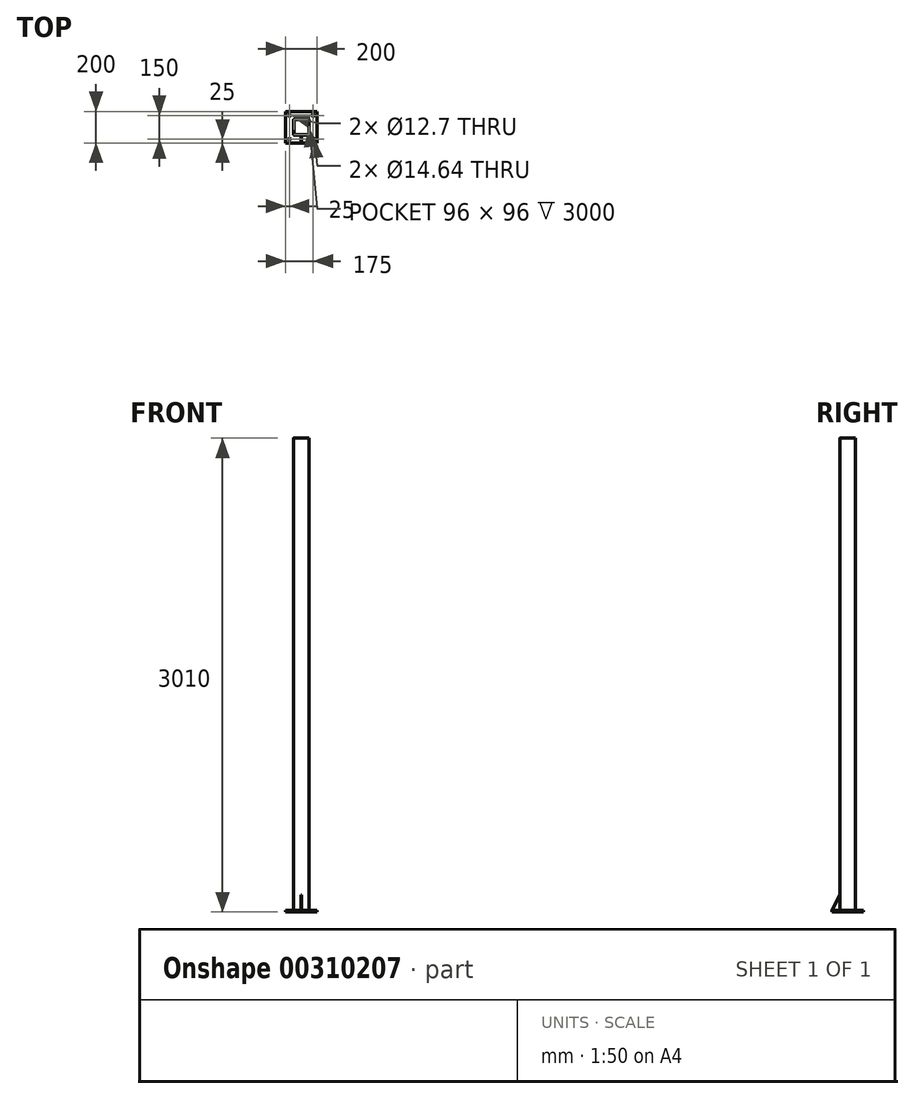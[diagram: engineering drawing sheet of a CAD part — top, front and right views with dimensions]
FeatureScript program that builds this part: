
annotation { "Feature Type Name" : "Feature", "Feature Type Description" : "" }
export const myFeature = defineFeature(function(context is Context, id is Id, definition is map)
    precondition{}
    {
        {
            var Q0;
            Q0=qCreatedBy(makeId("Top.planeOp"),FACE);
            var sketch = newSketch(context, id + "F0", { "sketchPlane" : qUnion([Q0])});
            skLineSegment(sketch, "E0.bottom", {"start": v(100, 100) * mm, "end": v(-100, 100) * mm});
            skLineSegment(sketch, "E0.top", {"start": v(100, -100) * mm, "end": v(-100, -100) * mm});
            skLineSegment(sketch, "E0.left", {"start": v(100, 100) * mm, "end": v(100, -100) * mm});
            skLineSegment(sketch, "E0.right", {"start": v(-100, 100) * mm, "end": v(-100, -100) * mm});
            skPoint(sketch, "E0.middle", {"position": v(0, 0) * mm});
            skCircle(sketch, "E1", {"center": v(-75, 75) * mm, "radius": 6.35 * mm});
            skCircle(sketch, "E2", {"center": v(75, 75) * mm, "radius": 7.32 * mm});
            skCircle(sketch, "E3.MirrorC", {"center": v(-75, -75) * mm, "radius": 6.35 * mm});
            skCircle(sketch, "E4.MirrorC", {"center": v(75, -75) * mm, "radius": 7.32 * mm});
            skSolve(sketch);
        }
        {
            var Q0;
            Q0=makeQuery(id+"F0.imprint","IMPRINT",FACE,{"disambiguationData":[TD([[makeQuery(id+"F0.imprint","IMPRINT",EDGE,{"derivedFrom":sQuery(id+"F0.wireOp",EDGE,"E0.bottom")}),1.0]])]});
            extrude(context, id + "F1", {"entities" : qUnion([Q0]), "depth" : 10 * mm});
        }
        {
            var Q0;
            Q0=makeQuery(id+"F1.opExtrude","CAP_FACE",FACE,{"disambiguationData":[OSD([sQuery(id+"F0.wireOp",EDGE,"E0.bottom"),sQuery(id+"F0.wireOp",EDGE,"E0.top"),sQuery(id+"F0.wireOp",EDGE,"E0.left"),sQuery(id+"F0.wireOp",EDGE,"E0.right"),sQuery(id+"F0.wireOp",EDGE,"E1"),sQuery(id+"F0.wireOp",EDGE,"E2"),sQuery(id+"F0.wireOp",EDGE,"E3.MirrorC"),sQuery(id+"F0.wireOp",EDGE,"E4.MirrorC")])],"isStart":false});
            var sketch = newSketch(context, id + "F2", { "sketchPlane" : qUnion([Q0])});
            skLineSegment(sketch, "E5.bottom", {"start": v(48, 50) * mm, "end": v(-48, 50) * mm});
            skLineSegment(sketch, "E5.top", {"start": v(48, -50) * mm, "end": v(-48, -50) * mm});
            skLineSegment(sketch, "E5.left", {"start": v(50, 48) * mm, "end": v(50, -48) * mm});
            skLineSegment(sketch, "E5.right", {"start": v(-50, 48) * mm, "end": v(-50, -48) * mm});
            skPoint(sketch, "E5.middle", {"position": v(0, 0) * mm});
            skLineSegment(sketch, "E6.0", {"start": v(48, 48) * mm, "end": v(-48, 48) * mm});
            skLineSegment(sketch, "E7.0", {"start": v(-95, -95) * mm, "end": v(95, -95) * mm});
            skLineSegment(sketch, "E7.1", {"start": v(-95, 95) * mm, "end": v(-95, -95) * mm});
            skLineSegment(sketch, "E7.2", {"start": v(95, 95) * mm, "end": v(-95, 95) * mm});
            skLineSegment(sketch, "E7.3", {"start": v(95, -95) * mm, "end": v(95, 95) * mm});
            skLineSegment(sketch, "E8.0", {"start": v(48, 48) * mm, "end": v(48, -48) * mm});
            skLineSegment(sketch, "E9.0", {"start": v(-48, 48) * mm, "end": v(-48, -48) * mm});
            skLineSegment(sketch, "E10.0", {"start": v(48, -48) * mm, "end": v(-48, -48) * mm});
            skPoint(sketch, "E11.visualSharp", {"position": v(-50, 50) * mm});
            skArc(sketch, "E11.filletArc", {"start": v(-48, 50) * mm, "mid": v(-49.41, 49.41) * mm, "end": v(-50, 48) * mm});
            skPoint(sketch, "E12.visualSharp", {"position": v(50, 50) * mm});
            skArc(sketch, "E12.filletArc", {"start": v(50, 48) * mm, "mid": v(49.41, 49.41) * mm, "end": v(48, 50) * mm});
            skPoint(sketch, "E13.visualSharp", {"position": v(50, -50) * mm});
            skArc(sketch, "E13.filletArc", {"start": v(48, -50) * mm, "mid": v(49.41, -49.41) * mm, "end": v(50, -48) * mm});
            skPoint(sketch, "E14.visualSharp", {"position": v(-50, -50) * mm});
            skArc(sketch, "E14.filletArc", {"start": v(-50, -48) * mm, "mid": v(-49.41, -49.41) * mm, "end": v(-48, -50) * mm});
            skSolve(sketch);
        }
        {
            var Q0;
            Q0=makeQuery(id+"F2.imprint","IMPRINT",FACE,{"disambiguationData":[TD([[makeQuery(id+"F2.imprint","IMPRINT",EDGE,{"derivedFrom":sQuery(id+"F2.wireOp",EDGE,"E5.bottom")}),1.0]])]});
            extrude(context, id + "F3", {"entities" : qUnion([Q0]), "operationType" : NewBodyOperationType.ADD, "depth" : 3000 * mm});
        }
        {
            var Q0;
            Q0=qCreatedBy(makeId("Right.planeOp"),FACE);
            var sketch = newSketch(context, id + "F4", { "sketchPlane" : qUnion([Q0])});
            skLineSegment(sketch, "E15", {"start": v(-100, 10) * mm, "end": v(-50, 110) * mm});
            skLineSegment(sketch, "E16", {"start": v(-50, 110) * mm, "end": v(-50, 10) * mm});
            skLineSegment(sketch, "E17", {"start": v(-50, 10) * mm, "end": v(-100, 10) * mm});
            skSolve(sketch);
        }
        {
            var Q0;
            Q0 = qSketchRegion(id + "F4", true);
            extrude(context, id + "F5", {"entities" : qUnion([Q0]), "operationType" : NewBodyOperationType.ADD, "depth" : 2.5 * mm, "hasSecondDirection" : true, "secondDirectionOppositeDirection" : true, "secondDirectionDepth" : 2.5 * mm});
        }
    });
